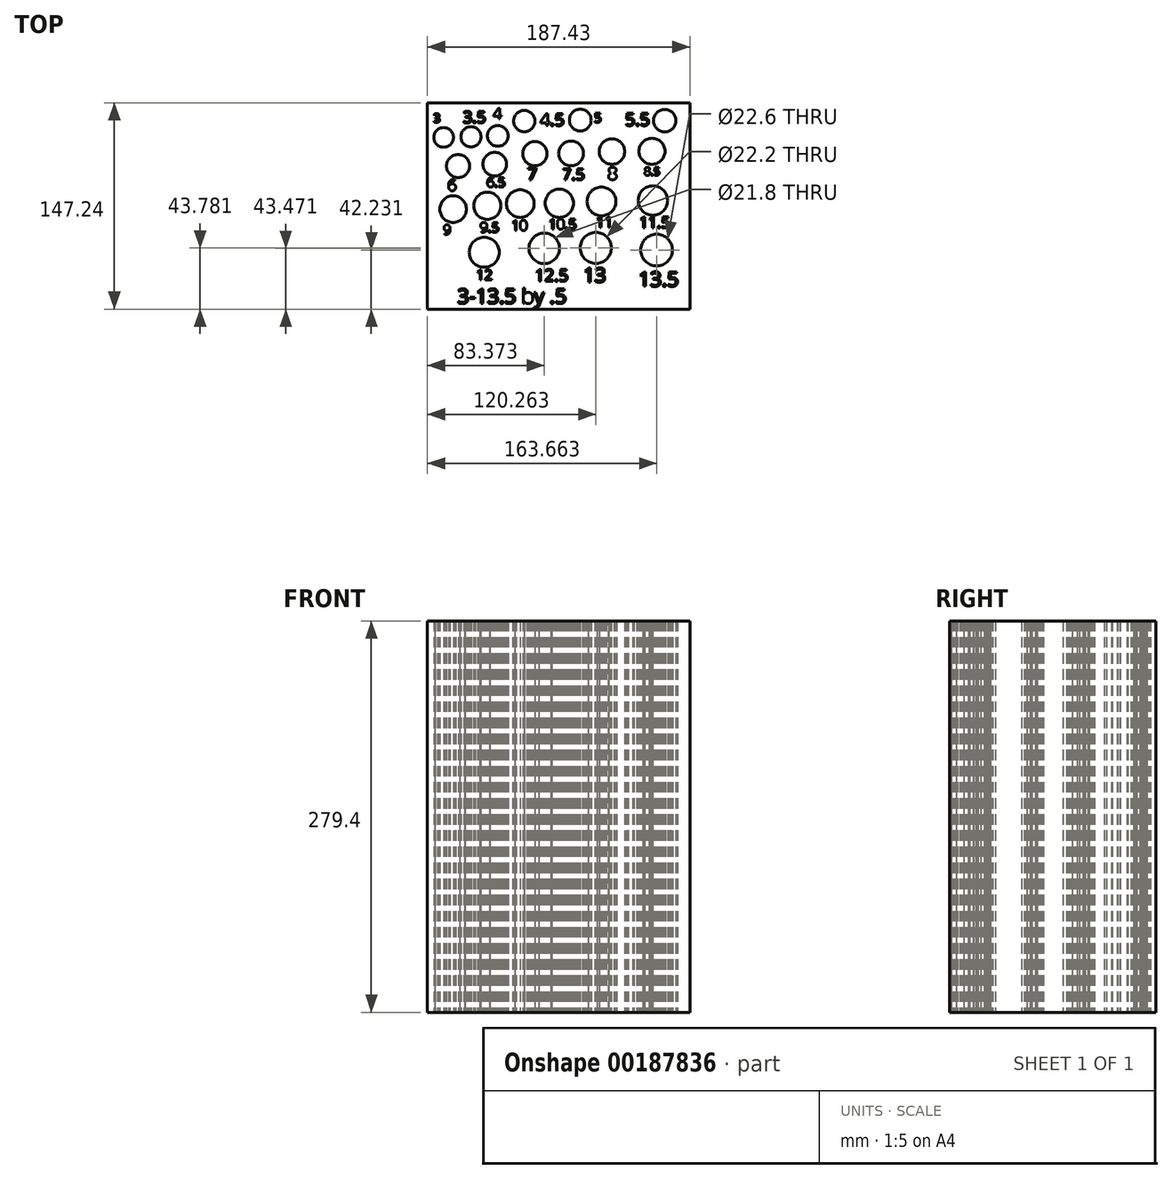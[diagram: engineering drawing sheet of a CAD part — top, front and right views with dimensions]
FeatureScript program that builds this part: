
annotation { "Feature Type Name" : "Feature", "Feature Type Description" : "" }
export const myFeature = defineFeature(function(context is Context, id is Id, definition is map)
    precondition{}
    {
        {
            var Q0;
            Q0=qCreatedBy(makeId("Top.planeOp"),FACE);
            var sketch = newSketch(context, id + "F0", { "sketchPlane" : qUnion([Q0])});
            skCircle(sketch, "E0", {"center": v(-65.2, 51.22) * mm, "radius": 7 * mm});
            skCircle(sketch, "E1", {"center": v(-45.64, 51.65) * mm, "radius": 7.2 * mm});
            skCircle(sketch, "E2", {"center": v(-26.51, 52.31) * mm, "radius": 7.4 * mm});
            skCircle(sketch, "E3", {"center": v(32.4, 63.52) * mm, "radius": 7.8 * mm});
            skCircle(sketch, "E4", {"center": v(92.74, 63.17) * mm, "radius": 8 * mm});
            skCircle(sketch, "E5", {"center": v(-54.87, 30.77) * mm, "radius": 8.22 * mm});
            skCircle(sketch, "E6", {"center": v(-28.71, 32.1) * mm, "radius": 8.45 * mm});
            skCircle(sketch, "E7", {"center": v(0, 39.57) * mm, "radius": 8.65 * mm});
            skCircle(sketch, "E8", {"center": v(25.8, 39.79) * mm, "radius": 8.85 * mm});
            skCircle(sketch, "E9", {"center": v(55.03, 41.1) * mm, "radius": 9.1 * mm});
            skCircle(sketch, "E10", {"center": v(83.6, 41.32) * mm, "radius": 9.3 * mm});
            skCircle(sketch, "E11", {"center": v(-58.39, 0) * mm, "radius": 9.5 * mm});
            skCircle(sketch, "E12", {"center": v(-33.99, 2.42) * mm, "radius": 9.7 * mm});
            skCircle(sketch, "E13", {"center": v(-10.47, 3.96) * mm, "radius": 9.9 * mm});
            skCircle(sketch, "E14", {"center": v(17.45, 4.18) * mm, "radius": 10.1 * mm});
            skCircle(sketch, "E15", {"center": v(47.56, 5.5) * mm, "radius": 10.3 * mm});
            skCircle(sketch, "E16", {"center": v(84.27, 6.15) * mm, "radius": 10.5 * mm});
            skLineSegment(sketch, "E17.bottom", {"start": v(-76.7, 75.8) * mm, "end": v(110.72, 75.8) * mm});
            skLineSegment(sketch, "E17.top", {"start": v(-76.7, -71.43) * mm, "end": v(110.72, -71.43) * mm});
            skLineSegment(sketch, "E17.left", {"start": v(-76.7, 75.8) * mm, "end": v(-76.7, -71.43) * mm});
            skLineSegment(sketch, "E17.right", {"start": v(110.72, 75.8) * mm, "end": v(110.72, -71.43) * mm});
            skCircle(sketch, "E18", {"center": v(-36.19, -30.77) * mm, "radius": 10.7 * mm});
            skCircle(sketch, "E19", {"center": v(6.66, -27.96) * mm, "radius": 10.9 * mm});
            skCircle(sketch, "E20", {"center": v(43.55, -27.65) * mm, "radius": 11.1 * mm});
            skCircle(sketch, "E21", {"center": v(86.95, -29.2) * mm, "radius": 11.3 * mm});
            skText(sketch, "E22", { "text": "3-13.5 by .5", "fontName": "OpenSans-Regular.ttf"});
            skText(sketch, "E23", { "text": "13.5", "fontName": "OpenSans-Regular.ttf"});
            skText(sketch, "E24", { "text": "13", "fontName": "OpenSans-Regular.ttf"});
            skText(sketch, "E25", { "text": "12.5", "fontName": "OpenSans-Regular.ttf"});
            skText(sketch, "E26", { "text": "12", "fontName": "OpenSans-Regular.ttf"});
            skText(sketch, "E27", { "text": "11.5", "fontName": "OpenSans-Regular.ttf"});
            skText(sketch, "E28", { "text": "11", "fontName": "OpenSans-Regular.ttf"});
            skText(sketch, "E29", { "text": "10.5", "fontName": "OpenSans-Regular.ttf"});
            skText(sketch, "E30", { "text": "10", "fontName": "OpenSans-Regular.ttf"});
            skText(sketch, "E31", { "text": "9.5", "fontName": "OpenSans-Regular.ttf"});
            skText(sketch, "E32", { "text": "9", "fontName": "OpenSans-Regular.ttf"});
            skText(sketch, "E33", { "text": "8.5", "fontName": "OpenSans-Regular.ttf"});
            skText(sketch, "E34", { "text": "8", "fontName": "OpenSans-Regular.ttf"});
            skText(sketch, "E35", { "text": "7.5", "fontName": "OpenSans-Regular.ttf"});
            skText(sketch, "E36", { "text": "7", "fontName": "OpenSans-Regular.ttf"});
            skText(sketch, "E37", { "text": "6.5", "fontName": "OpenSans-Regular.ttf"});
            skText(sketch, "E38", { "text": "6", "fontName": "OpenSans-Regular.ttf"});
            skText(sketch, "E39", { "text": "5.5", "fontName": "OpenSans-Regular.ttf"});
            skText(sketch, "E40", { "text": "5", "fontName": "OpenSans-Regular.ttf"});
            skText(sketch, "E41", { "text": "4.5", "fontName": "OpenSans-Regular.ttf"});
            skCircle(sketch, "E42", {"center": v(-7.61, 62.86) * mm, "radius": 7.6 * mm});
            skText(sketch, "E43", { "text": "4", "fontName": "OpenSans-Regular.ttf"});
            skText(sketch, "E44", { "text": "3.5", "fontName": "OpenSans-Regular.ttf"});
            skText(sketch, "E45", { "text": "3", "fontName": "OpenSans-Regular.ttf"});
            const initialGuessF0  = {"E22": [-0.05535, -0.06734, 1, 0, 0.0105], "E23": [0.07396, -0.05513, 1, 0, 0.01045], "E24": [0.03456, -0.05214, 1, 0, 0.01023], "E25": [0, -0.05152, 1, 0, 0.00868], "E26": [-0.0419, -0.05056, 1, 0, 0.00725], "E27": [0.0746, -0.0134, 1, 0, 0.00791], "E28": [0.0436, -0.01297, 1, 0, 0.0077], "E29": [0.00975, -0.01429, 1, 0, 0.00725], "E30": [-0.01684, -0.01517, 1, 0, 0.00725], "E31": [-0.03926, -0.01649, 1, 0, 0.00703], "E32": [-0.06542, -0.01802, 1, 0, 0.00681], "E33": [0.07811, 0.02418, 1, 0, 0.00571], "E34": [0.05196, 0.0211, 1, 0, 0.0088], "E35": [0.01965, 0.02088, 1, 0, 0.00813], "E36": [-0.00541, 0.02088, 1, 0, 0.00857], "E37": [-0.03443, 0.01583, 1, 0, 0.00681], "E38": [-0.06234, 0.01319, 1, 0, 0.00791], "E39": [0.06449, 0.05957, 1, 0, 0.00901], "E40": [0.04229, 0.06199, 1, 0, 0.0066], "E41": [0.00382, 0.05957, 1, 0, 0.0088], "E43": [-0.02981, 0.0644, 1, 0, 0.0077], "E44": [-0.05135, 0.06155, 1, 0, 0.00835], "E45": [-0.07245, 0.06199, 1, 0, 0.00615]};
            skSetInitialGuess(sketch, initialGuessF0);
            skSolve(sketch);
        }
        {
            var Q0;
            Q0 = qSketchRegion(id + "F0", true);
            extrude(context, id + "F1", {"entities" : qUnion([Q0]), "depth" : 279.4 * mm});
        }
    });
